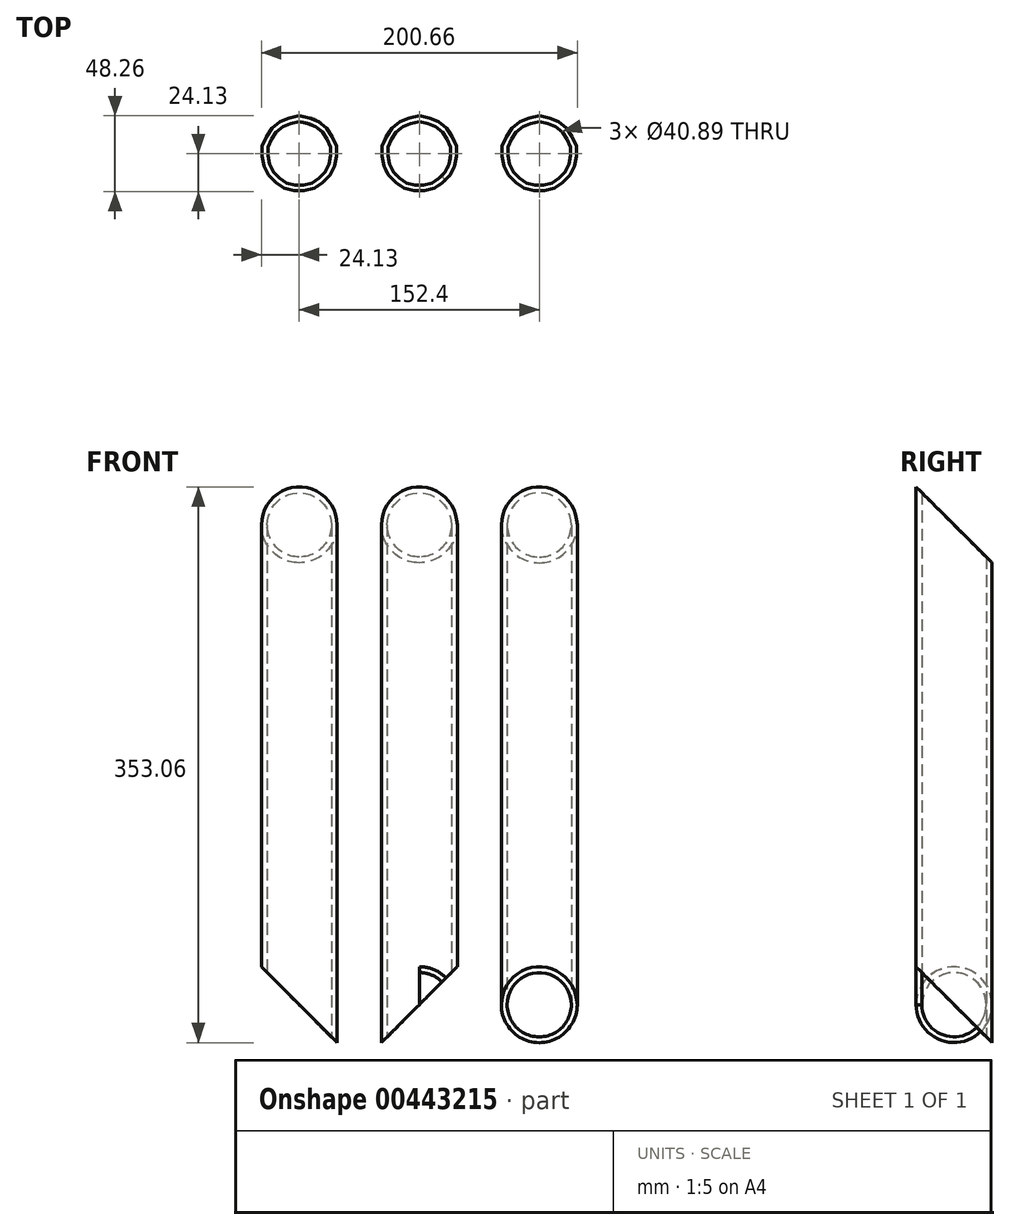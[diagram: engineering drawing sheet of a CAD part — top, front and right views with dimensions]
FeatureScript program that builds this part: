
annotation { "Feature Type Name" : "Feature", "Feature Type Description" : "" }
export const myFeature = defineFeature(function(context is Context, id is Id, definition is map)
    precondition{}
    {
        {
            var Q0;
            Q0=qCreatedBy(makeId("Top.planeOp"),FACE);
            var sketch = newSketch(context, id + "F0", { "sketchPlane" : qUnion([Q0])});
            skCircle(sketch, "E0", {"center": v(0, 0) * mm, "radius": 24.13 * mm});
            skCircle(sketch, "E1", {"center": v(0, 0) * mm, "radius": 20.45 * mm});
            skSolve(sketch);
        }
        {
            var Q0;
            Q0 = qSketchRegion(id + "F0", true);
            extrude(context, id + "F1", {"entities" : qUnion([Q0]), "endBound" : BoundingType.SYMMETRIC, "depth" : 762 * mm});
        }
        {
            var Q0;
            Q0=qCreatedBy(makeId("Top.planeOp"),FACE);
            var sketch = newSketch(context, id + "F2", { "sketchPlane" : qUnion([Q0])});
            skCircle(sketch, "E2", {"center": v(-76.2, 0) * mm, "radius": 24.13 * mm});
            skCircle(sketch, "E3", {"center": v(-76.2, 0) * mm, "radius": 20.45 * mm});
            skSolve(sketch);
        }
        {
            var Q0;
            Q0 = qSketchRegion(id + "F2", true);
            var Q1;
            Q1=makeQuery(id+"F2.imprint","IMPRINT",FACE,{"disambiguationData":[TD([[makeQuery(id+"F2.imprint","IMPRINT",EDGE,{"derivedFrom":sQuery(id+"F2.wireOp",EDGE,"E2")}),1.0]])]});
            extrude(context, id + "F3", {"entities" : qUnion([Q0, Q1]), "endBound" : BoundingType.SYMMETRIC, "depth" : 457.2 * mm});
        }
        {
            var Q0;
            Q0=qCreatedBy(makeId("Front.planeOp"),FACE);
            var sketch = newSketch(context, id + "F4", { "sketchPlane" : qUnion([Q0])});
            skLineSegment(sketch, "E4", {"start": v(0, -152.4) * mm, "end": v(76.2, -76.2) * mm});
            skLineSegment(sketch, "E5", {"start": v(76.2, -76.2) * mm, "end": v(440.95, -406.4) * mm});
            skLineSegment(sketch, "E6", {"start": v(440.95, -406.4) * mm, "end": v(-403.88, -406.4) * mm});
            skLineSegment(sketch, "E7", {"start": v(-403.88, -406.4) * mm, "end": v(-76.2, -228.6) * mm});
            skLineSegment(sketch, "E8", {"start": v(-76.2, -228.6) * mm, "end": v(0, -152.4) * mm});
            skSolve(sketch);
        }
        {
            var Q0;
            Q0 = qSketchRegion(id + "F4", true);
            extrude(context, id + "F5", {"entities" : qUnion([Q0]), "operationType" : NewBodyOperationType.REMOVE, "endBound" : BoundingType.SYMMETRIC, "oppositeDirection" : true, "depth" : 152.4 * mm});
        }
        {
            var Q0;
            Q0=qCreatedBy(makeId("Right.planeOp"),FACE);
            var sketch = newSketch(context, id + "F6", { "sketchPlane" : qUnion([Q0])});
            skLineSegment(sketch, "E9", {"start": v(0, 152.4) * mm, "end": v(-76.2, 228.6) * mm});
            skLineSegment(sketch, "E10", {"start": v(-76.2, 228.6) * mm, "end": v(-76.2, 457.2) * mm});
            skLineSegment(sketch, "E11", {"start": v(-76.2, 457.2) * mm, "end": v(76.2, 457.2) * mm});
            skLineSegment(sketch, "E12", {"start": v(76.2, 457.2) * mm, "end": v(76.2, 76.2) * mm});
            skLineSegment(sketch, "E13", {"start": v(76.2, 76.2) * mm, "end": v(0, 152.4) * mm});
            skSolve(sketch);
        }
        {
            var Q0;
            Q0 = qSketchRegion(id + "F6", true);
            extrude(context, id + "F7", {"entities" : qUnion([Q0]), "operationType" : NewBodyOperationType.REMOVE, "endBound" : BoundingType.SYMMETRIC, "oppositeDirection" : true, "depth" : 152.4 * mm});
        }
        {
            var Q0;
            Q0=qCreatedBy(makeId("Top.planeOp"),FACE);
            var sketch = newSketch(context, id + "F8", { "sketchPlane" : qUnion([Q0])});
            skCircle(sketch, "E14", {"center": v(76.2, 0) * mm, "radius": 24.13 * mm});
            skCircle(sketch, "E15", {"center": v(76.2, 0) * mm, "radius": 20.45 * mm});
            skSolve(sketch);
        }
        {
            var Q0;
            Q0=makeQuery(id+"F8.imprint","IMPRINT",FACE,{"disambiguationData":[TD([[makeQuery(id+"F8.imprint","IMPRINT",EDGE,{"derivedFrom":sQuery(id+"F8.wireOp",EDGE,"E14")}),1.0]])]});
            extrude(context, id + "F9", {"entities" : qUnion([Q0]), "endBound" : BoundingType.SYMMETRIC, "depth" : 508 * mm});
        }
        {
            var Q0;
            Q0=qCreatedBy(makeId("Right.planeOp"),FACE);
            var sketch = newSketch(context, id + "F10", { "sketchPlane" : qUnion([Q0])});
            skLineSegment(sketch, "E16", {"start": v(0, 152.4) * mm, "end": v(76.2, 76.2) * mm});
            skLineSegment(sketch, "E17", {"start": v(76.2, 76.2) * mm, "end": v(76.2, 304.8) * mm});
            skLineSegment(sketch, "E18", {"start": v(76.2, 304.8) * mm, "end": v(-76.2, 304.8) * mm});
            skLineSegment(sketch, "E19", {"start": v(-76.2, 304.8) * mm, "end": v(-76.2, 228.6) * mm});
            skLineSegment(sketch, "E20", {"start": v(-76.2, 228.6) * mm, "end": v(0, 152.4) * mm});
            skSolve(sketch);
        }
        {
            var Q0;
            Q0 = qSketchRegion(id + "F10", true);
            extrude(context, id + "F11", {"entities" : qUnion([Q0]), "operationType" : NewBodyOperationType.REMOVE, "endBound" : BoundingType.SYMMETRIC, "oppositeDirection" : true, "depth" : 304.8 * mm});
        }
        {
            var Q0;
            Q0=qCreatedBy(makeId("Front.planeOp"),FACE);
            var sketch = newSketch(context, id + "F12", { "sketchPlane" : qUnion([Q0])});
            skLineSegment(sketch, "E21", {"start": v(-76.2, 158) * mm, "end": v(-76.2, -278.06) * mm});
            skLineSegment(sketch, "E22", {"start": v(-76.2, -152.4) * mm, "end": v(-152.4, -76.2) * mm});
            skLineSegment(sketch, "E23", {"start": v(-152.4, -76.2) * mm, "end": v(-152.4, -304.8) * mm});
            skLineSegment(sketch, "E24", {"start": v(-152.4, -304.8) * mm, "end": v(0, -304.8) * mm});
            skLineSegment(sketch, "E25", {"start": v(0, -304.8) * mm, "end": v(0, -228.6) * mm});
            skLineSegment(sketch, "E26", {"start": v(0, -228.6) * mm, "end": v(-76.2, -152.4) * mm});
            skSolve(sketch);
        }
        {
            var Q0;
            Q0=makeQuery(id+"F12.imprint","IMPRINT",FACE,{"disambiguationData":[TD([[makeQuery(id+"F12.imprint","IMPRINT",EDGE,{"derivedFrom":sQuery(id+"F12.wireOp",EDGE,"E22")}),1.0]])]});
            extrude(context, id + "F13", {"entities" : qUnion([Q0]), "operationType" : NewBodyOperationType.REMOVE, "endBound" : BoundingType.SYMMETRIC, "oppositeDirection" : true, "depth" : 152.4 * mm});
        }
        {
            var Q0;
            Q0=qCreatedBy(makeId("Right.planeOp"),FACE);
            cPlane(context, id + "F14", {"entities" : qUnion([Q0]), "cplaneType" : CPlaneType.OFFSET, "offset" : 76.2 * mm, "width" : 152.4 * mm, "height" : 152.4 * mm});
        }
        {
            var Q0;
            Q0=qCreatedBy(id+"F14.planeOp",FACE);
            var sketch = newSketch(context, id + "F15", { "sketchPlane" : qUnion([Q0])});
            skLineSegment(sketch, "E27", {"start": v(0, -152.4) * mm, "end": v(76.2, -228.6) * mm});
            skLineSegment(sketch, "E28", {"start": v(76.2, -228.6) * mm, "end": v(76.2, -304.8) * mm});
            skLineSegment(sketch, "E29", {"start": v(76.2, -304.8) * mm, "end": v(-76.2, -304.8) * mm});
            skLineSegment(sketch, "E30", {"start": v(-76.2, -304.8) * mm, "end": v(-76.2, -76.2) * mm});
            skLineSegment(sketch, "E31", {"start": v(-76.2, -76.2) * mm, "end": v(0, -152.4) * mm});
            skSolve(sketch);
        }
        {
            var Q0;
            Q0 = qSketchRegion(id + "F15", true);
            extrude(context, id + "F16", {"entities" : qUnion([Q0]), "operationType" : NewBodyOperationType.REMOVE, "endBound" : BoundingType.SYMMETRIC, "oppositeDirection" : true, "depth" : 152.4 * mm});
        }
    });
